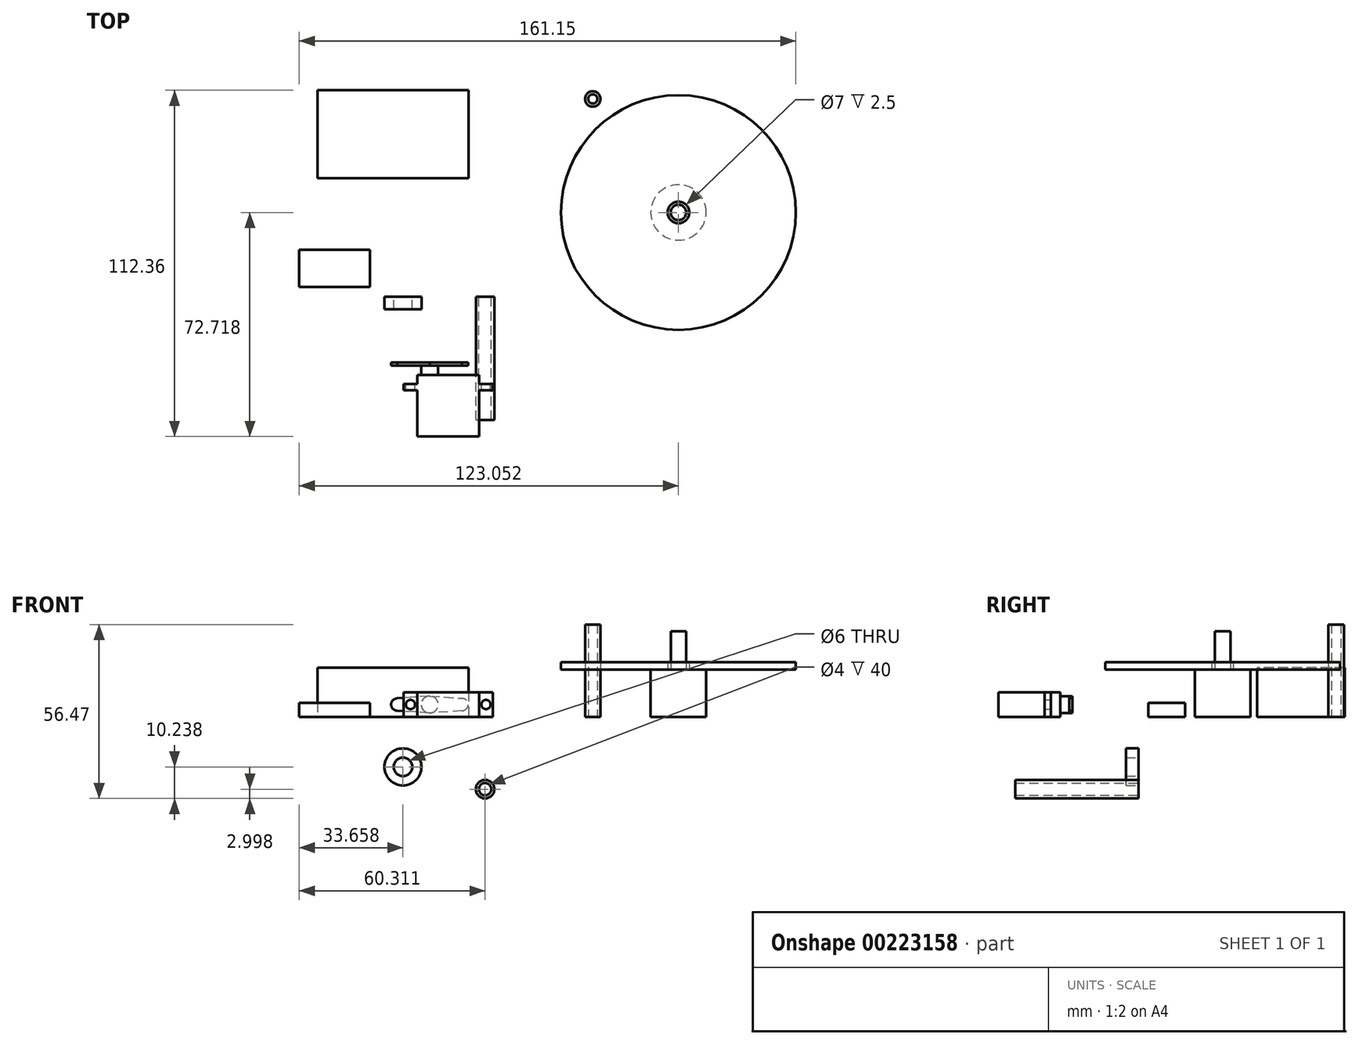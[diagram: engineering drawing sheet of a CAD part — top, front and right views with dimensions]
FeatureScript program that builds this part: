
annotation { "Feature Type Name" : "Feature", "Feature Type Description" : "" }
export const myFeature = defineFeature(function(context is Context, id is Id, definition is map)
    precondition{}
    {
        {
            var Q0;
            Q0=qCreatedBy(makeId("Top.planeOp"),FACE);
            var sketch = newSketch(context, id + "F0", { "sketchPlane" : qUnion([Q0])});
            skCircle(sketch, "E0", {"center": v(8.32, 64.19) * mm, "radius": 2.5 * mm});
            skCircle(sketch, "E1", {"center": v(8.32, 64.19) * mm, "radius": 1.5 * mm});
            skSolve(sketch);
        }
        {
            var Q0;
            Q0 = qSketchRegion(id + "F0", true);
            extrude(context, id + "F1", {"entities" : qUnion([Q0]), "depth" : 30 * mm});
        }
        {
            var Q0;
            Q0=qCreatedBy(makeId("Top.planeOp"),FACE);
            var sketch = newSketch(context, id + "F2", { "sketchPlane" : qUnion([Q0])});
            skCircle(sketch, "E2", {"center": v(36.12, 27.36) * mm, "radius": 9 * mm});
            skSolve(sketch);
        }
        {
            var Q0;
            Q0 = qSketchRegion(id + "F2", true);
            extrude(context, id + "F3", {"entities" : qUnion([Q0]), "depth" : 15.3 * mm});
        }
        {
            var Q0;
            Q0=makeQuery(id+"F3.opExtrude","CAP_FACE",FACE,{"disambiguationData":[OSD([sQuery(id+"F2.wireOp",EDGE,"E2")])],"isStart":false});
            var sketch = newSketch(context, id + "F4", { "sketchPlane" : qUnion([Q0])});
            skCircle(sketch, "E3", {"center": v(36.12, 27.36) * mm, "radius": 2.5 * mm});
            skSolve(sketch);
        }
        {
            var Q0;
            Q0 = qSketchRegion(id + "F4", true);
            extrude(context, id + "F5", {"entities" : qUnion([Q0]), "operationType" : NewBodyOperationType.ADD, "depth" : 12.5 * mm});
        }
        {
            var Q0;
            Q0=makeQuery(id+"F3.opExtrude","CAP_FACE",FACE,{"disambiguationData":[OSD([sQuery(id+"F2.wireOp",EDGE,"E2")])],"isStart":false});
            var sketch = newSketch(context, id + "F6", { "sketchPlane" : qUnion([Q0])});
            skCircle(sketch, "E4", {"center": v(36.12, 27.36) * mm, "radius": 3.5 * mm});
            skCircle(sketch, "E5", {"center": v(36.12, 27.36) * mm, "radius": 38.1 * mm});
            skSolve(sketch);
        }
        {
            var Q0;
            Q0 = qSketchRegion(id + "F6", true);
            extrude(context, id + "F7", {"entities" : qUnion([Q0]), "operationType" : NewBodyOperationType.ADD, "depth" : 2.5 * mm});
        }
        {
            var Q0;
            Q0=qCreatedBy(makeId("Top.planeOp"),FACE);
            var sketch = newSketch(context, id + "F8", { "sketchPlane" : qUnion([Q0])});
            skLineSegment(sketch, "E6.bottom", {"start": v(-48.6, -25.36) * mm, "end": v(-28.6, -25.36) * mm});
            skLineSegment(sketch, "E6.top", {"start": v(-48.6, -45.36) * mm, "end": v(-28.6, -45.36) * mm});
            skLineSegment(sketch, "E6.left", {"start": v(-48.6, -25.36) * mm, "end": v(-48.6, -45.36) * mm});
            skLineSegment(sketch, "E6.right", {"start": v(-28.6, -25.36) * mm, "end": v(-28.6, -45.36) * mm});
            skSolve(sketch);
        }
        {
            var Q0;
            Q0 = qSketchRegion(id + "F8", true);
            extrude(context, id + "F9", {"entities" : qUnion([Q0]), "depth" : 8 * mm});
        }
        {
            var Q0;
            Q0=makeQuery(id+"F9.opExtrude","SWEPT_FACE",FACE,{"disambiguationData":[OSD([sQuery(id+"F8.wireOp",EDGE,"E6.right")])]});
            var sketch = newSketch(context, id + "F10", { "sketchPlane" : qUnion([Q0])});
            skLineSegment(sketch, "E7.bottom", {"start": v(-30.36, 0) * mm, "end": v(-28.36, 0) * mm});
            skLineSegment(sketch, "E7.top", {"start": v(-30.36, 8) * mm, "end": v(-28.36, 8) * mm});
            skLineSegment(sketch, "E7.left", {"start": v(-30.36, 0) * mm, "end": v(-30.36, 8) * mm});
            skLineSegment(sketch, "E7.right", {"start": v(-28.36, 0) * mm, "end": v(-28.36, 8) * mm});
            skSolve(sketch);
        }
        {
            var Q0;
            Q0 = qSketchRegion(id + "F10", true);
            extrude(context, id + "F11", {"entities" : qUnion([Q0]), "operationType" : NewBodyOperationType.ADD, "depth" : 4.5 * mm});
        }
        {
            var Q0;
            Q0=makeQuery(id+"F9.opExtrude","SWEPT_FACE",FACE,{"disambiguationData":[OSD([sQuery(id+"F8.wireOp",EDGE,"E6.left")])]});
            var sketch = newSketch(context, id + "F12", { "sketchPlane" : qUnion([Q0])});
            skLineSegment(sketch, "E8.bottom", {"start": v(28.36, 0) * mm, "end": v(30.36, 0) * mm});
            skLineSegment(sketch, "E8.top", {"start": v(28.36, 8) * mm, "end": v(30.36, 8) * mm});
            skLineSegment(sketch, "E8.left", {"start": v(28.36, 0) * mm, "end": v(28.36, 8) * mm});
            skLineSegment(sketch, "E8.right", {"start": v(30.36, 0) * mm, "end": v(30.36, 8) * mm});
            skSolve(sketch);
        }
        {
            var Q0;
            Q0 = qSketchRegion(id + "F12", true);
            extrude(context, id + "F13", {"entities" : qUnion([Q0]), "operationType" : NewBodyOperationType.ADD, "depth" : 4.5 * mm});
        }
        {
            var Q0;
            Q0=makeQuery(id+"F9.opExtrude","SWEPT_FACE",FACE,{"disambiguationData":[OSD([sQuery(id+"F8.wireOp",EDGE,"E6.bottom")])]});
            var sketch = newSketch(context, id + "F14", { "sketchPlane" : qUnion([Q0])});
            skCircle(sketch, "E9", {"center": v(44.6, 4) * mm, "radius": 2.75 * mm});
            skSolve(sketch);
        }
        {
            var Q0;
            Q0 = qSketchRegion(id + "F14", true);
            extrude(context, id + "F15", {"entities" : qUnion([Q0]), "operationType" : NewBodyOperationType.ADD, "depth" : 4 * mm});
        }
        {
            var Q0;
            Q0=makeQuery(id+"F13.opExtrude","SWEPT_FACE",FACE,{"disambiguationData":[OSD([sQuery(id+"F12.wireOp",EDGE,"E8.left")])]});
            var sketch = newSketch(context, id + "F16", { "sketchPlane" : qUnion([Q0])});
            skCircle(sketch, "E10", {"center": v(50.85, 4) * mm, "radius": 1.5 * mm});
            skPoint(sketch, "E10.centerSnap0", {"position": v(53.1, 4) * mm});
            skPoint(sketch, "E10.centerSnap1", {"position": v(50.85, 8) * mm});
            skCircle(sketch, "E11", {"center": v(26.35, 4) * mm, "radius": 1.5 * mm});
            skSolve(sketch);
        }
        {
            var Q0;
            Q0 = qSketchRegion(id + "F16", true);
            extrude(context, id + "F17", {"entities" : qUnion([Q0]), "operationType" : NewBodyOperationType.REMOVE, "endBound" : BoundingType.THROUGH_ALL, "oppositeDirection" : true, "depth" : 25 * mm});
        }
        {
            var Q0;
            Q0=qCreatedBy(makeId("Top.planeOp"),FACE);
            var sketch = newSketch(context, id + "F18", { "sketchPlane" : qUnion([Q0])});
            skLineSegment(sketch, "E12.bottom", {"start": v(-81.03, 67) * mm, "end": v(-32.03, 67) * mm});
            skLineSegment(sketch, "E12.top", {"start": v(-81.03, 38.5) * mm, "end": v(-32.03, 38.5) * mm});
            skLineSegment(sketch, "E12.left", {"start": v(-81.03, 67) * mm, "end": v(-81.03, 38.5) * mm});
            skLineSegment(sketch, "E12.right", {"start": v(-32.03, 67) * mm, "end": v(-32.03, 38.5) * mm});
            skSolve(sketch);
        }
        {
            var Q0;
            Q0 = qSketchRegion(id + "F18", true);
            extrude(context, id + "F19", {"entities" : qUnion([Q0]), "depth" : 16 * mm});
        }
        {
            var Q0;
            Q0=makeQuery(id+"F15.opExtrude","CAP_FACE",FACE,{"disambiguationData":[OSD([sQuery(id+"F14.wireOp",EDGE,"E9")])],"isStart":false});
            var sketch = newSketch(context, id + "F20", { "sketchPlane" : qUnion([Q0])});
            skLineSegment(sketch, "E13", {"start": v(44.6, 6.76) * mm, "end": v(34.1, 6) * mm});
            skArc(sketch, "E14", {"start": v(34.1, 6) * mm, "mid": v(32.12, 4) * mm, "end": v(34.1, 2) * mm});
            skLineSegment(sketch, "E15", {"start": v(44.6, 4) * mm, "end": v(44.6, 9.73) * mm, "construction": true});
            skLineSegment(sketch, "E16", {"start": v(44.6, 9.73) * mm, "end": v(44.6, -2.01) * mm, "construction": true});
            skLineSegment(sketch, "E17", {"start": v(34.1, 2) * mm, "end": v(44.6, 1.24) * mm});
            skLineSegment(sketch, "E18", {"start": v(44.6, 1.24) * mm, "end": v(55.1, 2) * mm});
            skLineSegment(sketch, "E19", {"start": v(44.6, 6.76) * mm, "end": v(55.1, 6) * mm});
            skArc(sketch, "E20", {"start": v(55.1, 6) * mm, "mid": v(57.12, 4) * mm, "end": v(55.1, 2) * mm});
            skSolve(sketch);
        }
        {
            var Q0;
            Q0 = qSketchRegion(id + "F20", true);
            extrude(context, id + "F21", {"entities" : qUnion([Q0]), "operationType" : NewBodyOperationType.ADD, "oppositeDirection" : true, "depth" : 1 * mm});
        }
        {
            var Q0;
            Q0=qCreatedBy(makeId("Top.planeOp"),FACE);
            var sketch = newSketch(context, id + "F22", { "sketchPlane" : qUnion([Q0])});
            skLineSegment(sketch, "E21.bottom", {"start": v(-86.93, 15.2) * mm, "end": v(-63.93, 15.2) * mm});
            skLineSegment(sketch, "E21.top", {"start": v(-86.93, 3.2) * mm, "end": v(-63.93, 3.2) * mm});
            skLineSegment(sketch, "E21.left", {"start": v(-86.93, 15.2) * mm, "end": v(-86.93, 3.2) * mm});
            skLineSegment(sketch, "E21.right", {"start": v(-63.93, 15.2) * mm, "end": v(-63.93, 3.2) * mm});
            skSolve(sketch);
        }
        {
            var Q0;
            Q0 = qSketchRegion(id + "F22", true);
            extrude(context, id + "F23", {"entities" : qUnion([Q0]), "depth" : 4.5 * mm});
        }
        {
            var Q0;
            Q0=qCreatedBy(makeId("Front.planeOp"),FACE);
            var sketch = newSketch(context, id + "F24", { "sketchPlane" : qUnion([Q0])});
            skCircle(sketch, "E22", {"center": v(-53.27, -16.23) * mm, "radius": 6 * mm});
            skCircle(sketch, "E23", {"center": v(-53.27, -16.23) * mm, "radius": 3 * mm});
            skSolve(sketch);
        }
        {
            var Q0;
            Q0 = qSketchRegion(id + "F24", true);
            extrude(context, id + "F25", {"entities" : qUnion([Q0]), "depth" : 4 * mm});
        }
        {
            var Q0;
            Q0=qCreatedBy(makeId("Front.planeOp"),FACE);
            var sketch = newSketch(context, id + "F26", { "sketchPlane" : qUnion([Q0])});
            skCircle(sketch, "E24", {"center": v(-26.62, -23.47) * mm, "radius": 3 * mm});
            skCircle(sketch, "E25", {"center": v(-26.62, -23.47) * mm, "radius": 2 * mm});
            skSolve(sketch);
        }
        {
            var Q0;
            Q0 = qSketchRegion(id + "F26", true);
            extrude(context, id + "F27", {"entities" : qUnion([Q0]), "depth" : 40 * mm});
        }
    });
